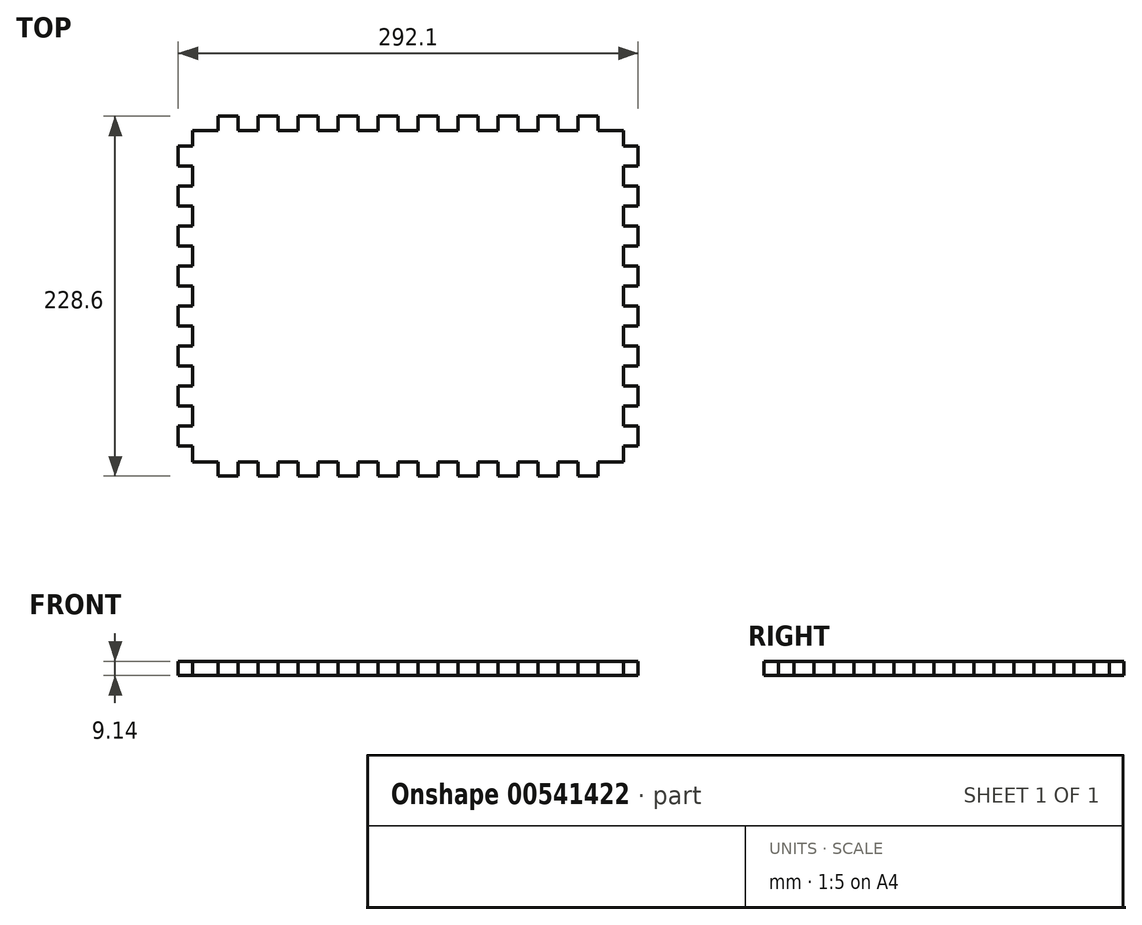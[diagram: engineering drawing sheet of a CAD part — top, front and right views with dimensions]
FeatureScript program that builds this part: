
annotation { "Feature Type Name" : "Feature", "Feature Type Description" : "" }
export const myFeature = defineFeature(function(context is Context, id is Id, definition is map)
    precondition{}
    {
        {
            var Q0;
            Q0=qCreatedBy(makeId("Top.planeOp"),FACE);
            var sketch = newSketch(context, id + "F0", { "sketchPlane" : qUnion([Q0])});
            skLineSegment(sketch, "E0.bottom", {"start": v(25.4, 0) * mm, "end": v(38.1, 0) * mm});
            skLineSegment(sketch, "E0.left", {"start": v(0, -19.05) * mm, "end": v(0, -31.75) * mm});
            skLineSegment(sketch, "E1", {"start": v(9.14, -9.14) * mm, "end": v(25.4, -9.14) * mm});
            skLineSegment(sketch, "E2", {"start": v(25.4, -9.14) * mm, "end": v(25.4, 0) * mm});
            skLineSegment(sketch, "E3", {"start": v(38.1, 0) * mm, "end": v(38.1, -9.14) * mm});
            skLineSegment(sketch, "E4", {"start": v(38.1, -9.14) * mm, "end": v(50.8, -9.14) * mm});
            skLineSegment(sketch, "E5", {"start": v(50.8, -9.14) * mm, "end": v(50.8, 0) * mm});
            skLineSegment(sketch, "E6", {"start": v(50.8, 0) * mm, "end": v(63.5, 0) * mm});
            skLineSegment(sketch, "E7", {"start": v(63.5, 0) * mm, "end": v(63.5, -9.14) * mm});
            skLineSegment(sketch, "E8", {"start": v(63.5, -9.14) * mm, "end": v(76.2, -9.14) * mm});
            skLineSegment(sketch, "E9", {"start": v(76.2, -9.14) * mm, "end": v(76.2, 0) * mm});
            skLineSegment(sketch, "E10", {"start": v(76.2, 0) * mm, "end": v(88.9, 0) * mm});
            skLineSegment(sketch, "E11", {"start": v(88.9, 0) * mm, "end": v(88.9, -9.14) * mm});
            skLineSegment(sketch, "E12", {"start": v(88.9, -9.14) * mm, "end": v(101.6, -9.14) * mm});
            skLineSegment(sketch, "E13", {"start": v(101.6, -9.14) * mm, "end": v(101.6, 0) * mm});
            skLineSegment(sketch, "E14.trimOffspring", {"start": v(101.6, 0) * mm, "end": v(114.3, 0) * mm});
            skLineSegment(sketch, "E15", {"start": v(114.3, 0) * mm, "end": v(114.3, -9.14) * mm});
            skLineSegment(sketch, "E16", {"start": v(114.3, -9.14) * mm, "end": v(127, -9.14) * mm});
            skLineSegment(sketch, "E17", {"start": v(127, -9.14) * mm, "end": v(127, 0) * mm});
            skLineSegment(sketch, "E18", {"start": v(127, 0) * mm, "end": v(139.7, 0) * mm});
            skLineSegment(sketch, "E19", {"start": v(139.7, 0) * mm, "end": v(139.7, -9.14) * mm});
            skLineSegment(sketch, "E20", {"start": v(139.7, -9.14) * mm, "end": v(152.4, -9.14) * mm});
            skLineSegment(sketch, "E21", {"start": v(152.4, -9.14) * mm, "end": v(152.4, 0) * mm});
            skLineSegment(sketch, "E22", {"start": v(152.4, 0) * mm, "end": v(165.1, 0) * mm});
            skLineSegment(sketch, "E23", {"start": v(165.1, 0) * mm, "end": v(165.1, -9.14) * mm});
            skLineSegment(sketch, "E24", {"start": v(165.1, -9.14) * mm, "end": v(177.8, -9.14) * mm});
            skLineSegment(sketch, "E25", {"start": v(177.8, -9.14) * mm, "end": v(177.8, 0) * mm});
            skLineSegment(sketch, "E26", {"start": v(177.8, 0) * mm, "end": v(190.5, 0) * mm});
            skLineSegment(sketch, "E27", {"start": v(190.5, 0) * mm, "end": v(190.5, -9.14) * mm});
            skLineSegment(sketch, "E28", {"start": v(190.5, -9.14) * mm, "end": v(203.2, -9.14) * mm});
            skLineSegment(sketch, "E29", {"start": v(203.2, -9.14) * mm, "end": v(203.2, 0) * mm});
            skLineSegment(sketch, "E30", {"start": v(203.2, 0) * mm, "end": v(215.9, 0) * mm});
            skLineSegment(sketch, "E31", {"start": v(215.9, 0) * mm, "end": v(215.9, -9.14) * mm});
            skLineSegment(sketch, "E32", {"start": v(215.9, -9.14) * mm, "end": v(228.6, -9.14) * mm});
            skLineSegment(sketch, "E33", {"start": v(228.6, -9.14) * mm, "end": v(228.6, 0) * mm});
            skLineSegment(sketch, "E34.trimOffspring", {"start": v(228.6, 0) * mm, "end": v(241.3, 0) * mm});
            skLineSegment(sketch, "E35", {"start": v(241.3, 0) * mm, "end": v(241.3, -9.14) * mm});
            skLineSegment(sketch, "E36", {"start": v(241.3, -9.14) * mm, "end": v(254, -9.14) * mm});
            skLineSegment(sketch, "E37", {"start": v(254, -9.14) * mm, "end": v(254, 0) * mm});
            skLineSegment(sketch, "E38", {"start": v(254, 0) * mm, "end": v(266.7, 0) * mm});
            skLineSegment(sketch, "E39", {"start": v(266.7, 0) * mm, "end": v(266.7, -9.14) * mm});
            skPoint(sketch, "E40.orphan", {"position": v(292.1, 0) * mm});
            skLineSegment(sketch, "E41", {"start": v(9.14, -9.14) * mm, "end": v(9.14, -19.05) * mm});
            skLineSegment(sketch, "E42", {"start": v(9.14, -19.05) * mm, "end": v(0, -19.05) * mm});
            skPoint(sketch, "E43.orphan", {"position": v(0, 0) * mm});
            skLineSegment(sketch, "E44", {"start": v(0, -31.75) * mm, "end": v(9.14, -31.75) * mm});
            skLineSegment(sketch, "E45", {"start": v(9.14, -31.75) * mm, "end": v(9.14, -44.45) * mm});
            skLineSegment(sketch, "E46", {"start": v(9.14, -44.45) * mm, "end": v(0, -44.45) * mm});
            skLineSegment(sketch, "E47", {"start": v(0, -44.45) * mm, "end": v(0, -57.15) * mm});
            skLineSegment(sketch, "E48", {"start": v(0, -57.15) * mm, "end": v(9.14, -57.15) * mm});
            skLineSegment(sketch, "E49", {"start": v(9.14, -57.15) * mm, "end": v(9.14, -69.85) * mm});
            skLineSegment(sketch, "E50", {"start": v(9.14, -69.85) * mm, "end": v(0, -69.85) * mm});
            skLineSegment(sketch, "E51", {"start": v(0, -69.85) * mm, "end": v(0, -82.55) * mm});
            skLineSegment(sketch, "E52", {"start": v(0, -82.55) * mm, "end": v(9.14, -82.55) * mm});
            skLineSegment(sketch, "E53", {"start": v(9.14, -82.55) * mm, "end": v(9.14, -95.25) * mm});
            skLineSegment(sketch, "E54", {"start": v(9.14, -95.25) * mm, "end": v(0, -95.25) * mm});
            skLineSegment(sketch, "E55", {"start": v(0, -95.25) * mm, "end": v(0, -107.95) * mm});
            skLineSegment(sketch, "E56", {"start": v(0, -107.95) * mm, "end": v(9.14, -107.95) * mm});
            skLineSegment(sketch, "E57", {"start": v(9.14, -107.95) * mm, "end": v(9.14, -120.65) * mm});
            skLineSegment(sketch, "E58", {"start": v(9.14, -120.65) * mm, "end": v(0, -120.65) * mm});
            skLineSegment(sketch, "E59.trimOffspring", {"start": v(0, -120.65) * mm, "end": v(0, -133.35) * mm});
            skLineSegment(sketch, "E60", {"start": v(0, -133.35) * mm, "end": v(9.14, -133.35) * mm});
            skLineSegment(sketch, "E61", {"start": v(9.14, -133.35) * mm, "end": v(9.14, -146.05) * mm});
            skLineSegment(sketch, "E62", {"start": v(9.14, -146.05) * mm, "end": v(0, -146.05) * mm});
            skLineSegment(sketch, "E63", {"start": v(0, -146.05) * mm, "end": v(0, -158.75) * mm});
            skLineSegment(sketch, "E64", {"start": v(0, -158.75) * mm, "end": v(9.14, -158.75) * mm});
            skLineSegment(sketch, "E65", {"start": v(9.14, -158.75) * mm, "end": v(9.14, -171.45) * mm});
            skLineSegment(sketch, "E66", {"start": v(9.14, -171.45) * mm, "end": v(0, -171.45) * mm});
            skLineSegment(sketch, "E67", {"start": v(0, -171.45) * mm, "end": v(0, -184.15) * mm});
            skLineSegment(sketch, "E68", {"start": v(0, -184.15) * mm, "end": v(9.14, -184.15) * mm});
            skLineSegment(sketch, "E69", {"start": v(9.14, -184.15) * mm, "end": v(9.14, -196.85) * mm});
            skLineSegment(sketch, "E70", {"start": v(9.14, -196.85) * mm, "end": v(0, -196.85) * mm});
            skPoint(sketch, "E71.orphan", {"position": v(0, -228.6) * mm});
            skLineSegment(sketch, "E72", {"start": v(146.05, -9.14) * mm, "end": v(146.05, -56.64) * mm, "construction": true});
            skLineSegment(sketch, "E73", {"start": v(0, -196.85) * mm, "end": v(0, -209.55) * mm});
            skLineSegment(sketch, "E74", {"start": v(0, -209.55) * mm, "end": v(9.14, -209.55) * mm});
            skLineSegment(sketch, "E75", {"start": v(9.14, -209.55) * mm, "end": v(9.14, -219.46) * mm});
            skLineSegment(sketch, "E76", {"start": v(9.14, -219.46) * mm, "end": v(25.4, -219.46) * mm});
            skLineSegment(sketch, "E77", {"start": v(25.4, -219.46) * mm, "end": v(25.4, -228.6) * mm});
            skLineSegment(sketch, "E78", {"start": v(9.14, -114.3) * mm, "end": v(67.99, -114.3) * mm, "construction": true});
            skLineSegment(sketch, "E79.MirrorCS", {"start": v(282.96, -9.14) * mm, "end": v(266.7, -9.14) * mm});
            skLineSegment(sketch, "E80.MirrorCS", {"start": v(282.96, -9.14) * mm, "end": v(282.96, -19.05) * mm});
            skLineSegment(sketch, "E81.MirrorCS", {"start": v(282.96, -19.05) * mm, "end": v(292.1, -19.05) * mm});
            skLineSegment(sketch, "E82.MirrorCS", {"start": v(292.1, -19.05) * mm, "end": v(292.1, -31.75) * mm});
            skLineSegment(sketch, "E83.MirrorCS", {"start": v(292.1, -31.75) * mm, "end": v(282.96, -31.75) * mm});
            skLineSegment(sketch, "E84.MirrorCS", {"start": v(282.96, -31.75) * mm, "end": v(282.96, -44.45) * mm});
            skLineSegment(sketch, "E85.MirrorCS", {"start": v(282.96, -44.45) * mm, "end": v(292.1, -44.45) * mm});
            skLineSegment(sketch, "E86.MirrorCS", {"start": v(292.1, -44.45) * mm, "end": v(292.1, -57.15) * mm});
            skLineSegment(sketch, "E87.MirrorCS", {"start": v(292.1, -57.15) * mm, "end": v(282.96, -57.15) * mm});
            skLineSegment(sketch, "E88.MirrorCS", {"start": v(282.96, -57.15) * mm, "end": v(282.96, -69.85) * mm});
            skLineSegment(sketch, "E89.MirrorCS", {"start": v(282.96, -69.85) * mm, "end": v(292.1, -69.85) * mm});
            skLineSegment(sketch, "E90.MirrorCS", {"start": v(292.1, -69.85) * mm, "end": v(292.1, -82.55) * mm});
            skLineSegment(sketch, "E91.MirrorCS", {"start": v(292.1, -82.55) * mm, "end": v(282.96, -82.55) * mm});
            skLineSegment(sketch, "E92.MirrorCS", {"start": v(282.96, -82.55) * mm, "end": v(282.96, -95.25) * mm});
            skLineSegment(sketch, "E93.MirrorCS", {"start": v(282.96, -95.25) * mm, "end": v(292.1, -95.25) * mm});
            skLineSegment(sketch, "E94.MirrorCS", {"start": v(292.1, -95.25) * mm, "end": v(292.1, -107.95) * mm});
            skLineSegment(sketch, "E95.MirrorCS", {"start": v(292.1, -107.95) * mm, "end": v(282.96, -107.95) * mm});
            skLineSegment(sketch, "E96.MirrorCS", {"start": v(282.96, -107.95) * mm, "end": v(282.96, -120.65) * mm});
            skLineSegment(sketch, "E97.MirrorCS", {"start": v(282.96, -120.65) * mm, "end": v(292.1, -120.65) * mm});
            skLineSegment(sketch, "E98.MirrorCS", {"start": v(292.1, -120.65) * mm, "end": v(292.1, -133.35) * mm});
            skLineSegment(sketch, "E99.MirrorCS", {"start": v(292.1, -133.35) * mm, "end": v(282.96, -133.35) * mm});
            skLineSegment(sketch, "E100.MirrorCS", {"start": v(282.96, -133.35) * mm, "end": v(282.96, -146.05) * mm});
            skLineSegment(sketch, "E101.MirrorCS", {"start": v(282.96, -146.05) * mm, "end": v(292.1, -146.05) * mm});
            skLineSegment(sketch, "E102.MirrorCS", {"start": v(292.1, -146.05) * mm, "end": v(292.1, -158.75) * mm});
            skLineSegment(sketch, "E103.MirrorCS", {"start": v(292.1, -158.75) * mm, "end": v(282.96, -158.75) * mm});
            skLineSegment(sketch, "E104.MirrorCS", {"start": v(282.96, -158.75) * mm, "end": v(282.96, -171.45) * mm});
            skLineSegment(sketch, "E105.MirrorCS", {"start": v(282.96, -171.45) * mm, "end": v(292.1, -171.45) * mm});
            skLineSegment(sketch, "E106.MirrorCS", {"start": v(292.1, -171.45) * mm, "end": v(292.1, -184.15) * mm});
            skLineSegment(sketch, "E107.MirrorCS", {"start": v(292.1, -184.15) * mm, "end": v(282.96, -184.15) * mm});
            skLineSegment(sketch, "E108.MirrorCS", {"start": v(282.96, -184.15) * mm, "end": v(282.96, -196.85) * mm});
            skLineSegment(sketch, "E109.MirrorCS", {"start": v(282.96, -196.85) * mm, "end": v(292.1, -196.85) * mm});
            skLineSegment(sketch, "E110.MirrorCS", {"start": v(292.1, -196.85) * mm, "end": v(292.1, -209.55) * mm});
            skLineSegment(sketch, "E111.MirrorCS", {"start": v(292.1, -209.55) * mm, "end": v(282.96, -209.55) * mm});
            skLineSegment(sketch, "E112.MirrorCS", {"start": v(282.96, -209.55) * mm, "end": v(282.96, -219.46) * mm});
            skLineSegment(sketch, "E113.MirrorCS", {"start": v(282.96, -219.46) * mm, "end": v(266.7, -219.46) * mm});
            skLineSegment(sketch, "E114.MirrorCS", {"start": v(266.7, -219.46) * mm, "end": v(266.7, -228.6) * mm});
            skLineSegment(sketch, "E115.MirrorCS", {"start": v(25.4, -228.6) * mm, "end": v(38.1, -228.6) * mm});
            skLineSegment(sketch, "E116.MirrorCS", {"start": v(38.1, -228.6) * mm, "end": v(38.1, -219.46) * mm});
            skLineSegment(sketch, "E117.MirrorCS", {"start": v(38.1, -219.46) * mm, "end": v(50.8, -219.46) * mm});
            skLineSegment(sketch, "E118.MirrorCS", {"start": v(50.8, -219.46) * mm, "end": v(50.8, -228.6) * mm});
            skLineSegment(sketch, "E119.MirrorCS", {"start": v(50.8, -228.6) * mm, "end": v(63.5, -228.6) * mm});
            skLineSegment(sketch, "E120.MirrorCS", {"start": v(63.5, -228.6) * mm, "end": v(63.5, -219.46) * mm});
            skLineSegment(sketch, "E121.MirrorCS", {"start": v(63.5, -219.46) * mm, "end": v(76.2, -219.46) * mm});
            skLineSegment(sketch, "E122.MirrorCS", {"start": v(76.2, -219.46) * mm, "end": v(76.2, -228.6) * mm});
            skLineSegment(sketch, "E123.MirrorCS", {"start": v(76.2, -228.6) * mm, "end": v(88.9, -228.6) * mm});
            skLineSegment(sketch, "E124.MirrorCS", {"start": v(88.9, -228.6) * mm, "end": v(88.9, -219.46) * mm});
            skLineSegment(sketch, "E125.MirrorCS", {"start": v(88.9, -219.46) * mm, "end": v(101.6, -219.46) * mm});
            skLineSegment(sketch, "E126.MirrorCS", {"start": v(101.6, -219.46) * mm, "end": v(101.6, -228.6) * mm});
            skLineSegment(sketch, "E127.MirrorCS", {"start": v(101.6, -228.6) * mm, "end": v(114.3, -228.6) * mm});
            skLineSegment(sketch, "E128.MirrorCS", {"start": v(114.3, -228.6) * mm, "end": v(114.3, -219.46) * mm});
            skLineSegment(sketch, "E129.MirrorCS", {"start": v(114.3, -219.46) * mm, "end": v(127, -219.46) * mm});
            skLineSegment(sketch, "E130.MirrorCS", {"start": v(127, -219.46) * mm, "end": v(127, -228.6) * mm});
            skLineSegment(sketch, "E131.MirrorCS", {"start": v(127, -228.6) * mm, "end": v(139.7, -228.6) * mm});
            skLineSegment(sketch, "E132.MirrorCS", {"start": v(139.7, -228.6) * mm, "end": v(139.7, -219.46) * mm});
            skLineSegment(sketch, "E133.MirrorCS", {"start": v(139.7, -219.46) * mm, "end": v(152.4, -219.46) * mm});
            skLineSegment(sketch, "E134.MirrorCS", {"start": v(152.4, -219.46) * mm, "end": v(152.4, -228.6) * mm});
            skLineSegment(sketch, "E135.MirrorCS", {"start": v(152.4, -228.6) * mm, "end": v(165.1, -228.6) * mm});
            skLineSegment(sketch, "E136.MirrorCS", {"start": v(165.1, -228.6) * mm, "end": v(165.1, -219.46) * mm});
            skLineSegment(sketch, "E137.MirrorCS", {"start": v(165.1, -219.46) * mm, "end": v(177.8, -219.46) * mm});
            skLineSegment(sketch, "E138.MirrorCS", {"start": v(177.8, -219.46) * mm, "end": v(177.8, -228.6) * mm});
            skLineSegment(sketch, "E139.MirrorCS", {"start": v(177.8, -228.6) * mm, "end": v(190.5, -228.6) * mm});
            skLineSegment(sketch, "E140.MirrorCS", {"start": v(190.5, -228.6) * mm, "end": v(190.5, -219.46) * mm});
            skLineSegment(sketch, "E141.MirrorCS", {"start": v(190.5, -219.46) * mm, "end": v(203.2, -219.46) * mm});
            skLineSegment(sketch, "E142.MirrorCS", {"start": v(203.2, -219.46) * mm, "end": v(203.2, -228.6) * mm});
            skLineSegment(sketch, "E143.MirrorCS", {"start": v(203.2, -228.6) * mm, "end": v(215.9, -228.6) * mm});
            skLineSegment(sketch, "E144.MirrorCS", {"start": v(215.9, -228.6) * mm, "end": v(215.9, -219.46) * mm});
            skLineSegment(sketch, "E145.MirrorCS", {"start": v(215.9, -219.46) * mm, "end": v(228.6, -219.46) * mm});
            skLineSegment(sketch, "E146.MirrorCS", {"start": v(228.6, -219.46) * mm, "end": v(228.6, -228.6) * mm});
            skLineSegment(sketch, "E147.MirrorCS", {"start": v(228.6, -228.6) * mm, "end": v(241.3, -228.6) * mm});
            skLineSegment(sketch, "E148.MirrorCS", {"start": v(241.3, -228.6) * mm, "end": v(241.3, -219.46) * mm});
            skLineSegment(sketch, "E149.MirrorCS", {"start": v(241.3, -219.46) * mm, "end": v(254, -219.46) * mm});
            skLineSegment(sketch, "E150.MirrorCS", {"start": v(254, -219.46) * mm, "end": v(254, -228.6) * mm});
            skLineSegment(sketch, "E151.MirrorCS", {"start": v(254, -228.6) * mm, "end": v(266.7, -228.6) * mm});
            skSolve(sketch);
        }
        {
            var Q0;
            Q0=makeQuery(id+"F0.imprint","IMPRINT",FACE,{"disambiguationData":[TD([[makeQuery(id+"F0.imprint","IMPRINT",EDGE,{"derivedFrom":sQuery(id+"F0.wireOp",EDGE,"E1")}),-1.0]])]});
            extrude(context, id + "F1", {"entities" : qUnion([Q0]), "depth" : 9.14 * mm, "offsetDistance" : 25.4 * mm});
        }
    });
